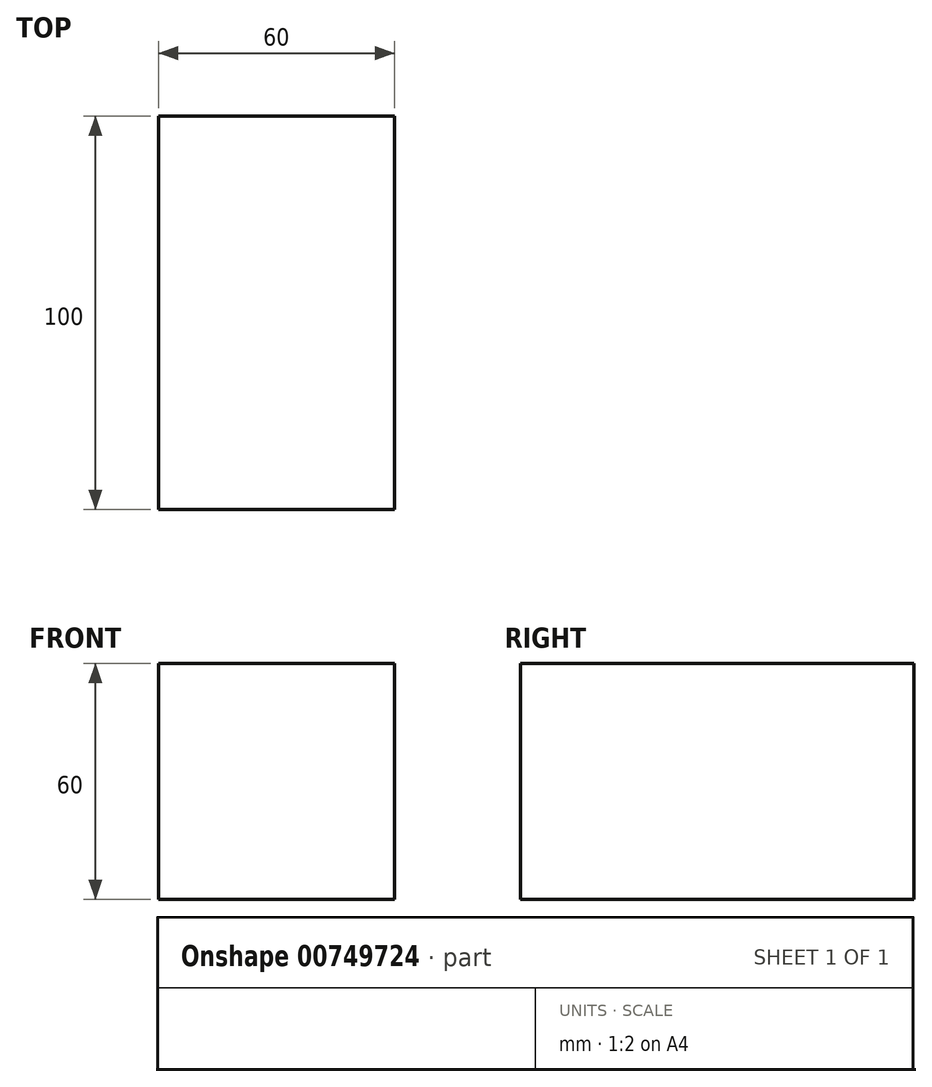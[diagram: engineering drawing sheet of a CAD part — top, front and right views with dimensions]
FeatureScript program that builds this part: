
annotation { "Feature Type Name" : "Feature", "Feature Type Description" : "" }
export const myFeature = defineFeature(function(context is Context, id is Id, definition is map)
    precondition{}
    {
        {
            var Q0;
            Q0=qCreatedBy(makeId("Front.planeOp"),FACE);
            var sketch = newSketch(context, id + "F0", { "sketchPlane" : qUnion([Q0])});
            skLineSegment(sketch, "E0.bottom", {"start": v(-30, 30) * mm, "end": v(30, 30) * mm});
            skLineSegment(sketch, "E0.top", {"start": v(-30, -30) * mm, "end": v(30, -30) * mm});
            skLineSegment(sketch, "E0.left", {"start": v(-30, 30) * mm, "end": v(-30, -30) * mm});
            skLineSegment(sketch, "E0.right", {"start": v(30, 30) * mm, "end": v(30, -30) * mm});
            skPoint(sketch, "E0.middle", {"position": v(0, 0) * mm});
            skSolve(sketch);
        }
        {
            var Q0;
            Q0=makeQuery(id+"F0.imprint","IMPRINT",FACE,{"disambiguationData":[TD([[makeQuery(id+"F0.imprint","IMPRINT",EDGE,{"derivedFrom":sQuery(id+"F0.wireOp",EDGE,"E0.bottom")}),-1.0]])]});
            extrude(context, id + "F1", {"entities" : qUnion([Q0]), "endBound" : BoundingType.SYMMETRIC, "depth" : 100 * mm, "offsetDistance" : 25 * mm});
        }
    });
